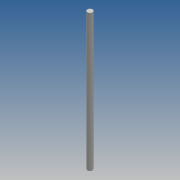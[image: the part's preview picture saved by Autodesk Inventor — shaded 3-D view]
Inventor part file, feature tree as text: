
AUTODESK INVENTOR PART (.ipt)
format: ipt  version: 2016 (Build 200138000, 138)  size: 67,072 bytes
history: native  units: mm
features: revolve x1, sketch x1
ambient origin geometry x8: Origin, YZ Plane, XZ Plane, XY Plane, X Axis, Y Axis, Z Axis, Center Point
bodies: Solid1 (feature_tree)
feature tree (2):
  revolve  "Revolution1"  [1 undecoded]
  sketch  "Sketch1"  dims[d0=4.0mm d1=110.0mm d2=90.0deg]
note: 1 required parameter value undecoded (feature->parameter linkage not recoverable at this tier; creation-order binding heuristic only, values carry confidence <= 0.55)
